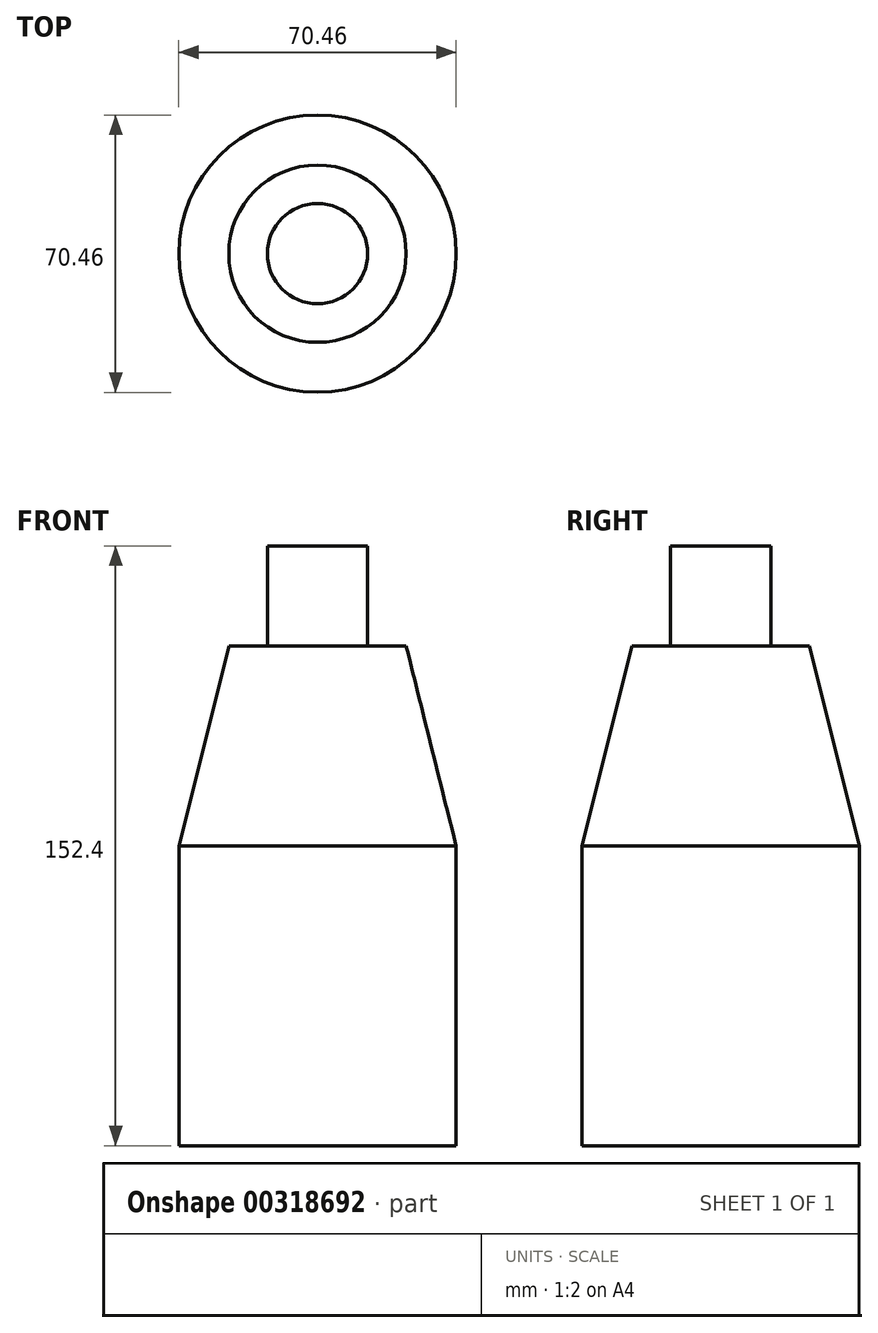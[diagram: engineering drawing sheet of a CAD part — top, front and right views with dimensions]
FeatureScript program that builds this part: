
annotation { "Feature Type Name" : "Feature", "Feature Type Description" : "" }
export const myFeature = defineFeature(function(context is Context, id is Id, definition is map)
    precondition{}
    {
        {
            var Q0;
            Q0=qCreatedBy(makeId("Top.planeOp"),FACE);
            var sketch = newSketch(context, id + "F0", { "sketchPlane" : qUnion([Q0])});
            skCircle(sketch, "E0", {"center": v(0, 0) * mm, "radius": 35.23 * mm});
            skSolve(sketch);
        }
        {
            var Q0;
            Q0=makeQuery(id+"F0.imprint","IMPRINT",FACE,{"disambiguationData":[TD([[makeQuery(id+"F0.imprint","IMPRINT",EDGE,{"derivedFrom":sQuery(id+"F0.wireOp",EDGE,"E0")}),1.0]])]});
            extrude(context, id + "F1", {"entities" : qUnion([Q0]), "depth" : 127 * mm});
        }
        {
            var Q0;
            Q0=makeQuery(id+"F1.opExtrude","CAP_EDGE",EDGE,{"disambiguationData":[OSD([sQuery(id+"F0.wireOp",EDGE,"E0")])],"isStart":false});
            chamfer(context, id + "F2", {"entities" : qUnion([Q0]), "chamferType" : ChamferType.TWO_OFFSETS, "width1" : 12.7 * mm, "oppositeDirection" : false, "width2" : 50.8 * mm, "tangentPropagation" : true});
        }
        {
            var Q0;
            Q0=makeQuery(id+"F1.opExtrude","CAP_FACE",FACE,{"disambiguationData":[OSD([sQuery(id+"F0.wireOp",EDGE,"E0")])],"isStart":false});
            var sketch = newSketch(context, id + "F3", { "sketchPlane" : qUnion([Q0])});
            skCircle(sketch, "E1", {"center": v(0, 0) * mm, "radius": 12.73 * mm});
            skSolve(sketch);
        }
        {
            var Q0;
            Q0=makeQuery(id+"F3.imprint","IMPRINT",FACE,{"disambiguationData":[TD([[makeQuery(id+"F3.imprint","IMPRINT",EDGE,{"derivedFrom":sQuery(id+"F3.wireOp",EDGE,"E1")}),1.0]])]});
            extrude(context, id + "F4", {"entities" : qUnion([Q0]), "operationType" : NewBodyOperationType.ADD, "depth" : 25.4 * mm});
        }
    });
